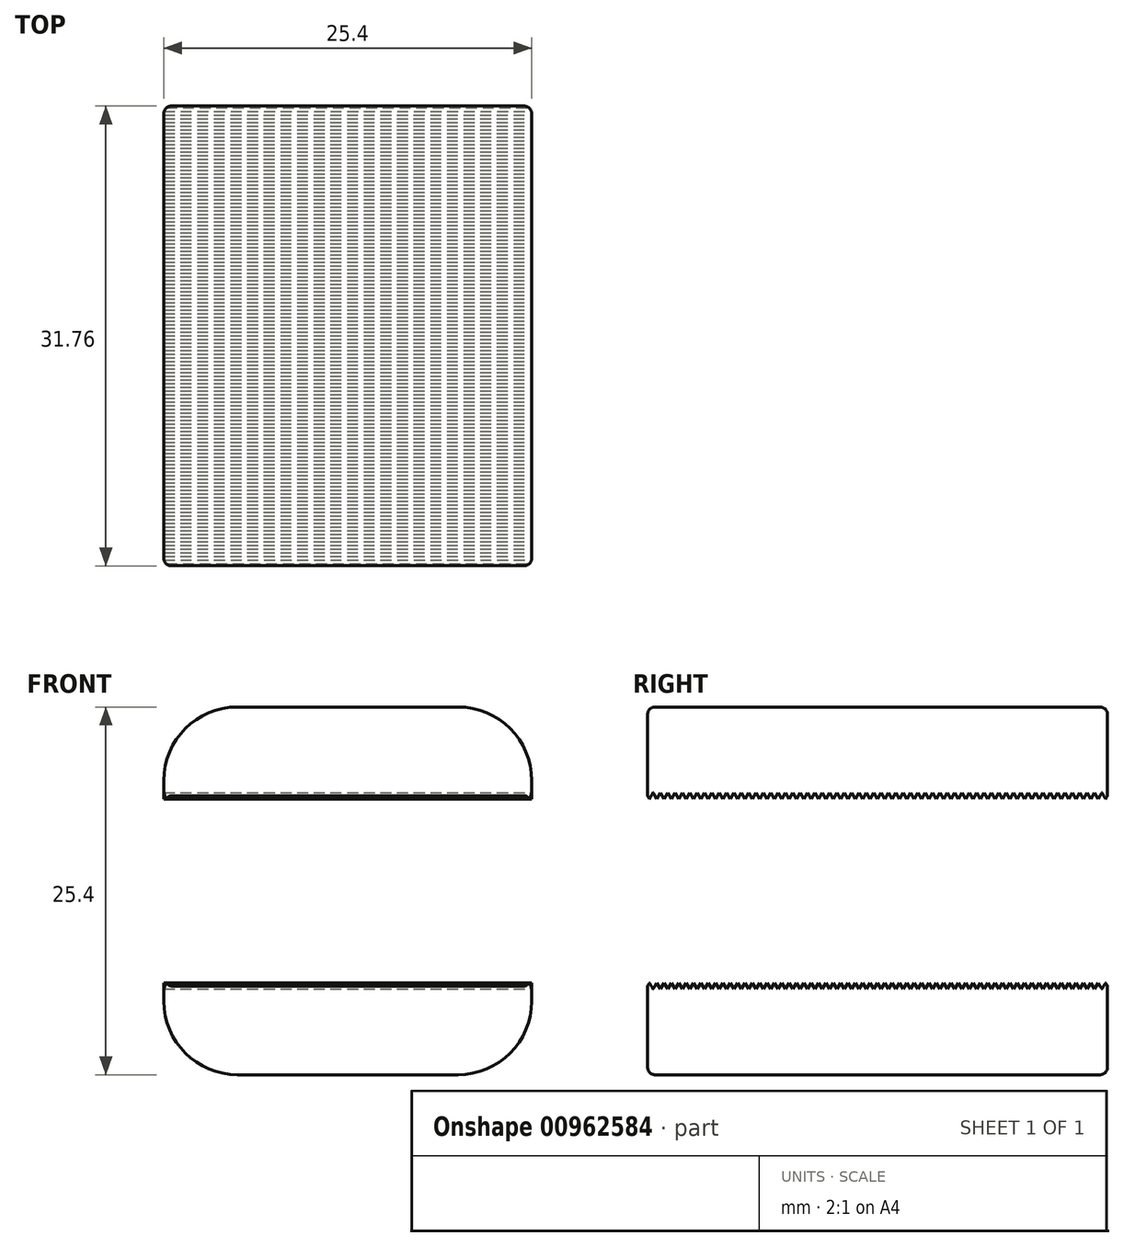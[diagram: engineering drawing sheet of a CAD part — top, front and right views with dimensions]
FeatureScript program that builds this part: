
annotation { "Feature Type Name" : "Feature", "Feature Type Description" : "" }
export const myFeature = defineFeature(function(context is Context, id is Id, definition is map)
    precondition{}
    {
        {
            var Q0;
            Q0=qCreatedBy(makeId("Front.planeOp"),FACE);
            var sketch = newSketch(context, id + "F0", { "sketchPlane" : qUnion([Q0])});
            skLineSegment(sketch, "E0.bottom", {"start": v(12.7, -12.7) * mm, "end": v(-12.7, -12.7) * mm});
            skLineSegment(sketch, "E0.top", {"start": v(12.7, 12.7) * mm, "end": v(-12.7, 12.7) * mm});
            skLineSegment(sketch, "E0.left", {"start": v(12.7, -12.7) * mm, "end": v(12.7, -6.35) * mm});
            skLineSegment(sketch, "E0.right", {"start": v(-12.7, -12.7) * mm, "end": v(-12.7, -6.35) * mm});
            skPoint(sketch, "E0.middle", {"position": v(0, 0) * mm});
            skLineSegment(sketch, "E1.bottom", {"start": v(12.7, -6.35) * mm, "end": v(-12.7, -6.35) * mm});
            skLineSegment(sketch, "E1.top", {"start": v(12.7, 6.35) * mm, "end": v(-12.7, 6.35) * mm});
            skLineSegment(sketch, "E2.trimOffspring", {"start": v(-12.7, 6.35) * mm, "end": v(-12.7, 12.7) * mm});
            skLineSegment(sketch, "E3.trimOffspring", {"start": v(12.7, 6.35) * mm, "end": v(12.7, 12.7) * mm});
            skSolve(sketch);
        }
        {
            var Q0;
            Q0=qSketchRegion(id+"F0",true);
            extrude(context, id + "F1", {"entities" : qUnion([Q0]), "endBound" : BoundingType.SYMMETRIC, "depth" : 31.75 * mm, "offsetDistance" : 25.4 * mm});
        }
        {
            var Q0;
            Q0=qCreatedBy(makeId("Right.planeOp"),FACE);
            var sketch = newSketch(context, id + "F2", { "sketchPlane" : qUnion([Q0])});
            skLineSegment(sketch, "E4", {"start": v(0, 6.35) * mm, "end": v(-0.25, 6.79) * mm});
            skLineSegment(sketch, "E5", {"start": v(-0.25, 6.79) * mm, "end": v(-0.5, 6.35) * mm});
            skLineSegment(sketch, "E6.1.0.0", {"start": v(-0.5, 6.35) * mm, "end": v(-0.76, 6.79) * mm});
            skLineSegment(sketch, "E6.1.0.1", {"start": v(-0.76, 6.79) * mm, "end": v(-1.02, 6.35) * mm});
            skLineSegment(sketch, "E6.2.0.0", {"start": v(-1.02, 6.35) * mm, "end": v(-1.27, 6.79) * mm});
            skLineSegment(sketch, "E6.2.0.1", {"start": v(-1.27, 6.79) * mm, "end": v(-1.52, 6.35) * mm});
            skLineSegment(sketch, "E6.3.0.0", {"start": v(-1.52, 6.35) * mm, "end": v(-1.78, 6.79) * mm});
            skLineSegment(sketch, "E6.3.0.1", {"start": v(-1.78, 6.79) * mm, "end": v(-2.03, 6.35) * mm});
            skLineSegment(sketch, "E6.4.0.0", {"start": v(-2.03, 6.35) * mm, "end": v(-2.29, 6.79) * mm});
            skLineSegment(sketch, "E6.4.0.1", {"start": v(-2.29, 6.79) * mm, "end": v(-2.54, 6.35) * mm});
            skLineSegment(sketch, "E6.5.0.0", {"start": v(-2.54, 6.35) * mm, "end": v(-2.8, 6.79) * mm});
            skLineSegment(sketch, "E6.5.0.1", {"start": v(-2.8, 6.79) * mm, "end": v(-3.05, 6.35) * mm});
            skLineSegment(sketch, "E6.6.0.0", {"start": v(-3.05, 6.35) * mm, "end": v(-3.3, 6.79) * mm});
            skLineSegment(sketch, "E6.6.0.1", {"start": v(-3.3, 6.79) * mm, "end": v(-3.56, 6.35) * mm});
            skLineSegment(sketch, "E6.7.0.0", {"start": v(-3.56, 6.35) * mm, "end": v(-3.81, 6.79) * mm});
            skLineSegment(sketch, "E6.7.0.1", {"start": v(-3.81, 6.79) * mm, "end": v(-4.06, 6.35) * mm});
            skLineSegment(sketch, "E6.8.0.0", {"start": v(-4.06, 6.35) * mm, "end": v(-4.32, 6.79) * mm});
            skLineSegment(sketch, "E6.8.0.1", {"start": v(-4.32, 6.79) * mm, "end": v(-4.57, 6.35) * mm});
            skLineSegment(sketch, "E6.9.0.0", {"start": v(-4.57, 6.35) * mm, "end": v(-4.83, 6.79) * mm});
            skLineSegment(sketch, "E6.9.0.1", {"start": v(-4.83, 6.79) * mm, "end": v(-5.08, 6.35) * mm});
            skLineSegment(sketch, "E6.10.0.0", {"start": v(-5.08, 6.35) * mm, "end": v(-5.33, 6.79) * mm});
            skLineSegment(sketch, "E6.10.0.1", {"start": v(-5.33, 6.79) * mm, "end": v(-5.59, 6.35) * mm});
            skLineSegment(sketch, "E6.11.0.0", {"start": v(-5.59, 6.35) * mm, "end": v(-5.84, 6.79) * mm});
            skLineSegment(sketch, "E6.11.0.1", {"start": v(-5.84, 6.79) * mm, "end": v(-6.1, 6.35) * mm});
            skLineSegment(sketch, "E6.12.0.0", {"start": v(-6.1, 6.35) * mm, "end": v(-6.35, 6.79) * mm});
            skLineSegment(sketch, "E6.12.0.1", {"start": v(-6.35, 6.79) * mm, "end": v(-6.6, 6.35) * mm});
            skLineSegment(sketch, "E6.13.0.0", {"start": v(-6.6, 6.35) * mm, "end": v(-6.86, 6.79) * mm});
            skLineSegment(sketch, "E6.13.0.1", {"start": v(-6.86, 6.79) * mm, "end": v(-7.11, 6.35) * mm});
            skLineSegment(sketch, "E6.14.0.0", {"start": v(-7.11, 6.35) * mm, "end": v(-7.37, 6.79) * mm});
            skLineSegment(sketch, "E6.14.0.1", {"start": v(-7.37, 6.79) * mm, "end": v(-7.62, 6.35) * mm});
            skLineSegment(sketch, "E6.15.0.0", {"start": v(-7.62, 6.35) * mm, "end": v(-7.87, 6.79) * mm});
            skLineSegment(sketch, "E6.15.0.1", {"start": v(-7.87, 6.79) * mm, "end": v(-8.13, 6.35) * mm});
            skLineSegment(sketch, "E6.16.0.0", {"start": v(-8.13, 6.35) * mm, "end": v(-8.38, 6.79) * mm});
            skLineSegment(sketch, "E6.16.0.1", {"start": v(-8.38, 6.79) * mm, "end": v(-8.64, 6.35) * mm});
            skLineSegment(sketch, "E6.17.0.0", {"start": v(-8.64, 6.35) * mm, "end": v(-8.9, 6.79) * mm});
            skLineSegment(sketch, "E6.17.0.1", {"start": v(-8.9, 6.79) * mm, "end": v(-9.14, 6.35) * mm});
            skLineSegment(sketch, "E6.18.0.0", {"start": v(-9.14, 6.35) * mm, "end": v(-9.4, 6.79) * mm});
            skLineSegment(sketch, "E6.18.0.1", {"start": v(-9.4, 6.79) * mm, "end": v(-9.65, 6.35) * mm});
            skLineSegment(sketch, "E6.19.0.0", {"start": v(-9.65, 6.35) * mm, "end": v(-9.9, 6.79) * mm});
            skLineSegment(sketch, "E6.19.0.1", {"start": v(-9.9, 6.79) * mm, "end": v(-10.16, 6.35) * mm});
            skLineSegment(sketch, "E6.20.0.0", {"start": v(-10.16, 6.35) * mm, "end": v(-10.41, 6.79) * mm});
            skLineSegment(sketch, "E6.20.0.1", {"start": v(-10.41, 6.79) * mm, "end": v(-10.67, 6.35) * mm});
            skLineSegment(sketch, "E6.21.0.0", {"start": v(-10.67, 6.35) * mm, "end": v(-10.92, 6.79) * mm});
            skLineSegment(sketch, "E6.21.0.1", {"start": v(-10.92, 6.79) * mm, "end": v(-11.18, 6.35) * mm});
            skLineSegment(sketch, "E6.22.0.0", {"start": v(-11.18, 6.35) * mm, "end": v(-11.43, 6.79) * mm});
            skLineSegment(sketch, "E6.22.0.1", {"start": v(-11.43, 6.79) * mm, "end": v(-11.68, 6.35) * mm});
            skLineSegment(sketch, "E6.23.0.0", {"start": v(-11.68, 6.35) * mm, "end": v(-11.94, 6.79) * mm});
            skLineSegment(sketch, "E6.23.0.1", {"start": v(-11.94, 6.79) * mm, "end": v(-12.2, 6.35) * mm});
            skLineSegment(sketch, "E6.24.0.0", {"start": v(-12.2, 6.35) * mm, "end": v(-12.45, 6.79) * mm});
            skLineSegment(sketch, "E6.24.0.1", {"start": v(-12.45, 6.79) * mm, "end": v(-12.7, 6.35) * mm});
            skLineSegment(sketch, "E6.direction1", {"start": v(-0.5, 6.35) * mm, "end": v(-1.02, 6.35) * mm, "construction": true});
            skLineSegment(sketch, "E7.0.25.0", {"start": v(-12.7, 6.35) * mm, "end": v(-12.95, 6.79) * mm});
            skLineSegment(sketch, "E7.3.25.0", {"start": v(-12.95, 6.79) * mm, "end": v(-13.2, 6.35) * mm});
            skLineSegment(sketch, "E7.0.26.0", {"start": v(-13.2, 6.35) * mm, "end": v(-13.46, 6.79) * mm});
            skLineSegment(sketch, "E7.3.26.0", {"start": v(-13.46, 6.79) * mm, "end": v(-13.72, 6.35) * mm});
            skLineSegment(sketch, "E7.0.27.0", {"start": v(-13.72, 6.35) * mm, "end": v(-13.97, 6.79) * mm});
            skLineSegment(sketch, "E7.3.27.0", {"start": v(-13.97, 6.79) * mm, "end": v(-14.22, 6.35) * mm});
            skLineSegment(sketch, "E7.0.28.0", {"start": v(-14.22, 6.35) * mm, "end": v(-14.48, 6.79) * mm});
            skLineSegment(sketch, "E7.3.28.0", {"start": v(-14.48, 6.79) * mm, "end": v(-14.73, 6.35) * mm});
            skLineSegment(sketch, "E7.0.29.0", {"start": v(-14.73, 6.35) * mm, "end": v(-14.99, 6.79) * mm});
            skLineSegment(sketch, "E7.3.29.0", {"start": v(-14.99, 6.79) * mm, "end": v(-15.24, 6.35) * mm});
            skLineSegment(sketch, "E7.0.30.0", {"start": v(-15.24, 6.35) * mm, "end": v(-15.5, 6.79) * mm});
            skLineSegment(sketch, "E7.3.30.0", {"start": v(-15.5, 6.79) * mm, "end": v(-15.75, 6.35) * mm});
            skLineSegment(sketch, "E7.0.31.0", {"start": v(-15.75, 6.35) * mm, "end": v(-16, 6.79) * mm});
            skLineSegment(sketch, "E7.3.31.0", {"start": v(-16, 6.79) * mm, "end": v(-16.26, 6.35) * mm});
            skLineSegment(sketch, "E7.0.32.0", {"start": v(-16.26, 6.35) * mm, "end": v(-16.51, 6.79) * mm});
            skLineSegment(sketch, "E7.3.32.0", {"start": v(-16.51, 6.79) * mm, "end": v(-16.76, 6.35) * mm});
            skLineSegment(sketch, "E7.0.33.0", {"start": v(-16.76, 6.35) * mm, "end": v(-17.02, 6.79) * mm});
            skLineSegment(sketch, "E7.3.33.0", {"start": v(-17.02, 6.79) * mm, "end": v(-17.27, 6.35) * mm});
            skLineSegment(sketch, "E7.0.34.0", {"start": v(-17.27, 6.35) * mm, "end": v(-17.53, 6.79) * mm});
            skLineSegment(sketch, "E7.3.34.0", {"start": v(-17.53, 6.79) * mm, "end": v(-17.78, 6.35) * mm});
            skLineSegment(sketch, "E7.0.35.0", {"start": v(-17.78, 6.35) * mm, "end": v(-18.03, 6.79) * mm});
            skLineSegment(sketch, "E7.3.35.0", {"start": v(-18.03, 6.79) * mm, "end": v(-18.29, 6.35) * mm});
            skLineSegment(sketch, "E7.0.36.0", {"start": v(-18.29, 6.35) * mm, "end": v(-18.54, 6.79) * mm});
            skLineSegment(sketch, "E7.3.36.0", {"start": v(-18.54, 6.79) * mm, "end": v(-18.8, 6.35) * mm});
            skLineSegment(sketch, "E7.0.37.0", {"start": v(-18.8, 6.35) * mm, "end": v(-19.05, 6.79) * mm});
            skLineSegment(sketch, "E7.3.37.0", {"start": v(-19.05, 6.79) * mm, "end": v(-19.3, 6.35) * mm});
            skLineSegment(sketch, "E7.0.38.0", {"start": v(-19.3, 6.35) * mm, "end": v(-19.56, 6.79) * mm});
            skLineSegment(sketch, "E7.3.38.0", {"start": v(-19.56, 6.79) * mm, "end": v(-19.81, 6.35) * mm});
            skLineSegment(sketch, "E7.0.39.0", {"start": v(-19.81, 6.35) * mm, "end": v(-20.07, 6.79) * mm});
            skLineSegment(sketch, "E7.3.39.0", {"start": v(-20.07, 6.79) * mm, "end": v(-20.32, 6.35) * mm});
            skLineSegment(sketch, "E8.1.0.0", {"start": v(0.25, 6.79) * mm, "end": v(0, 6.35) * mm});
            skLineSegment(sketch, "E8.1.0.1", {"start": v(0.5, 6.35) * mm, "end": v(0.25, 6.79) * mm});
            skLineSegment(sketch, "E8.2.0.0", {"start": v(0.76, 6.79) * mm, "end": v(0.5, 6.35) * mm});
            skLineSegment(sketch, "E8.2.0.1", {"start": v(1.02, 6.35) * mm, "end": v(0.76, 6.79) * mm});
            skLineSegment(sketch, "E8.3.0.0", {"start": v(1.27, 6.79) * mm, "end": v(1.02, 6.35) * mm});
            skLineSegment(sketch, "E8.3.0.1", {"start": v(1.52, 6.35) * mm, "end": v(1.27, 6.79) * mm});
            skLineSegment(sketch, "E8.4.0.0", {"start": v(1.78, 6.79) * mm, "end": v(1.52, 6.35) * mm});
            skLineSegment(sketch, "E8.4.0.1", {"start": v(2.03, 6.35) * mm, "end": v(1.78, 6.79) * mm});
            skLineSegment(sketch, "E8.5.0.0", {"start": v(2.29, 6.79) * mm, "end": v(2.03, 6.35) * mm});
            skLineSegment(sketch, "E8.5.0.1", {"start": v(2.54, 6.35) * mm, "end": v(2.29, 6.79) * mm});
            skLineSegment(sketch, "E8.6.0.0", {"start": v(2.8, 6.79) * mm, "end": v(2.54, 6.35) * mm});
            skLineSegment(sketch, "E8.6.0.1", {"start": v(3.05, 6.35) * mm, "end": v(2.8, 6.79) * mm});
            skLineSegment(sketch, "E8.7.0.0", {"start": v(3.3, 6.79) * mm, "end": v(3.05, 6.35) * mm});
            skLineSegment(sketch, "E8.7.0.1", {"start": v(3.56, 6.35) * mm, "end": v(3.3, 6.79) * mm});
            skLineSegment(sketch, "E8.8.0.0", {"start": v(3.81, 6.79) * mm, "end": v(3.56, 6.35) * mm});
            skLineSegment(sketch, "E8.8.0.1", {"start": v(4.06, 6.35) * mm, "end": v(3.81, 6.79) * mm});
            skLineSegment(sketch, "E8.9.0.0", {"start": v(4.32, 6.79) * mm, "end": v(4.06, 6.35) * mm});
            skLineSegment(sketch, "E8.9.0.1", {"start": v(4.57, 6.35) * mm, "end": v(4.32, 6.79) * mm});
            skLineSegment(sketch, "E8.10.0.0", {"start": v(4.83, 6.79) * mm, "end": v(4.57, 6.35) * mm});
            skLineSegment(sketch, "E8.10.0.1", {"start": v(5.08, 6.35) * mm, "end": v(4.83, 6.79) * mm});
            skLineSegment(sketch, "E8.11.0.0", {"start": v(5.33, 6.79) * mm, "end": v(5.08, 6.35) * mm});
            skLineSegment(sketch, "E8.11.0.1", {"start": v(5.59, 6.35) * mm, "end": v(5.33, 6.79) * mm});
            skLineSegment(sketch, "E8.12.0.0", {"start": v(5.84, 6.79) * mm, "end": v(5.59, 6.35) * mm});
            skLineSegment(sketch, "E8.12.0.1", {"start": v(6.1, 6.35) * mm, "end": v(5.84, 6.79) * mm});
            skLineSegment(sketch, "E8.13.0.0", {"start": v(6.35, 6.79) * mm, "end": v(6.1, 6.35) * mm});
            skLineSegment(sketch, "E8.13.0.1", {"start": v(6.6, 6.35) * mm, "end": v(6.35, 6.79) * mm});
            skLineSegment(sketch, "E8.14.0.0", {"start": v(6.86, 6.79) * mm, "end": v(6.6, 6.35) * mm});
            skLineSegment(sketch, "E8.14.0.1", {"start": v(7.11, 6.35) * mm, "end": v(6.86, 6.79) * mm});
            skLineSegment(sketch, "E8.15.0.0", {"start": v(7.37, 6.79) * mm, "end": v(7.11, 6.35) * mm});
            skLineSegment(sketch, "E8.15.0.1", {"start": v(7.62, 6.35) * mm, "end": v(7.37, 6.79) * mm});
            skLineSegment(sketch, "E8.16.0.0", {"start": v(7.87, 6.79) * mm, "end": v(7.62, 6.35) * mm});
            skLineSegment(sketch, "E8.16.0.1", {"start": v(8.13, 6.35) * mm, "end": v(7.87, 6.79) * mm});
            skLineSegment(sketch, "E8.17.0.0", {"start": v(8.38, 6.79) * mm, "end": v(8.13, 6.35) * mm});
            skLineSegment(sketch, "E8.17.0.1", {"start": v(8.64, 6.35) * mm, "end": v(8.38, 6.79) * mm});
            skLineSegment(sketch, "E8.18.0.0", {"start": v(8.9, 6.79) * mm, "end": v(8.64, 6.35) * mm});
            skLineSegment(sketch, "E8.18.0.1", {"start": v(9.14, 6.35) * mm, "end": v(8.9, 6.79) * mm});
            skLineSegment(sketch, "E8.19.0.0", {"start": v(9.4, 6.79) * mm, "end": v(9.14, 6.35) * mm});
            skLineSegment(sketch, "E8.19.0.1", {"start": v(9.65, 6.35) * mm, "end": v(9.4, 6.79) * mm});
            skLineSegment(sketch, "E8.20.0.0", {"start": v(9.9, 6.79) * mm, "end": v(9.65, 6.35) * mm});
            skLineSegment(sketch, "E8.20.0.1", {"start": v(10.16, 6.35) * mm, "end": v(9.9, 6.79) * mm});
            skLineSegment(sketch, "E8.21.0.0", {"start": v(10.41, 6.79) * mm, "end": v(10.16, 6.35) * mm});
            skLineSegment(sketch, "E8.21.0.1", {"start": v(10.67, 6.35) * mm, "end": v(10.41, 6.79) * mm});
            skLineSegment(sketch, "E8.22.0.0", {"start": v(10.92, 6.79) * mm, "end": v(10.67, 6.35) * mm});
            skLineSegment(sketch, "E8.22.0.1", {"start": v(11.18, 6.35) * mm, "end": v(10.92, 6.79) * mm});
            skLineSegment(sketch, "E8.23.0.0", {"start": v(11.43, 6.79) * mm, "end": v(11.18, 6.35) * mm});
            skLineSegment(sketch, "E8.23.0.1", {"start": v(11.68, 6.35) * mm, "end": v(11.43, 6.79) * mm});
            skLineSegment(sketch, "E8.24.0.0", {"start": v(11.94, 6.79) * mm, "end": v(11.68, 6.35) * mm});
            skLineSegment(sketch, "E8.24.0.1", {"start": v(12.2, 6.35) * mm, "end": v(11.94, 6.79) * mm});
            skLineSegment(sketch, "E8.25.0.0", {"start": v(12.45, 6.79) * mm, "end": v(12.2, 6.35) * mm});
            skLineSegment(sketch, "E8.25.0.1", {"start": v(12.7, 6.35) * mm, "end": v(12.45, 6.79) * mm});
            skLineSegment(sketch, "E8.26.0.0", {"start": v(12.95, 6.79) * mm, "end": v(12.7, 6.35) * mm});
            skLineSegment(sketch, "E8.26.0.1", {"start": v(13.2, 6.35) * mm, "end": v(12.95, 6.79) * mm});
            skLineSegment(sketch, "E8.27.0.0", {"start": v(13.46, 6.79) * mm, "end": v(13.2, 6.35) * mm});
            skLineSegment(sketch, "E8.27.0.1", {"start": v(13.72, 6.35) * mm, "end": v(13.46, 6.79) * mm});
            skLineSegment(sketch, "E8.28.0.0", {"start": v(13.97, 6.79) * mm, "end": v(13.72, 6.35) * mm});
            skLineSegment(sketch, "E8.28.0.1", {"start": v(14.22, 6.35) * mm, "end": v(13.97, 6.79) * mm});
            skLineSegment(sketch, "E8.29.0.0", {"start": v(14.48, 6.79) * mm, "end": v(14.22, 6.35) * mm});
            skLineSegment(sketch, "E8.29.0.1", {"start": v(14.73, 6.35) * mm, "end": v(14.48, 6.79) * mm});
            skLineSegment(sketch, "E8.30.0.0", {"start": v(14.99, 6.79) * mm, "end": v(14.73, 6.35) * mm});
            skLineSegment(sketch, "E8.30.0.1", {"start": v(15.24, 6.35) * mm, "end": v(14.99, 6.79) * mm});
            skLineSegment(sketch, "E8.31.0.0", {"start": v(15.5, 6.79) * mm, "end": v(15.24, 6.35) * mm});
            skLineSegment(sketch, "E8.31.0.1", {"start": v(15.75, 6.35) * mm, "end": v(15.5, 6.79) * mm});
            skLineSegment(sketch, "E8.32.0.0", {"start": v(16, 6.79) * mm, "end": v(15.75, 6.35) * mm});
            skLineSegment(sketch, "E8.32.0.1", {"start": v(16.26, 6.35) * mm, "end": v(16, 6.79) * mm});
            skLineSegment(sketch, "E8.33.0.0", {"start": v(16.51, 6.79) * mm, "end": v(16.26, 6.35) * mm});
            skLineSegment(sketch, "E8.33.0.1", {"start": v(16.76, 6.35) * mm, "end": v(16.51, 6.79) * mm});
            skLineSegment(sketch, "E8.34.0.0", {"start": v(17.02, 6.79) * mm, "end": v(16.76, 6.35) * mm});
            skLineSegment(sketch, "E8.34.0.1", {"start": v(17.27, 6.35) * mm, "end": v(17.02, 6.79) * mm});
            skLineSegment(sketch, "E8.35.0.0", {"start": v(17.53, 6.79) * mm, "end": v(17.27, 6.35) * mm});
            skLineSegment(sketch, "E8.35.0.1", {"start": v(17.78, 6.35) * mm, "end": v(17.53, 6.79) * mm});
            skLineSegment(sketch, "E8.36.0.0", {"start": v(18.03, 6.79) * mm, "end": v(17.78, 6.35) * mm});
            skLineSegment(sketch, "E8.36.0.1", {"start": v(18.29, 6.35) * mm, "end": v(18.03, 6.79) * mm});
            skLineSegment(sketch, "E8.37.0.0", {"start": v(18.54, 6.79) * mm, "end": v(18.29, 6.35) * mm});
            skLineSegment(sketch, "E8.37.0.1", {"start": v(18.8, 6.35) * mm, "end": v(18.54, 6.79) * mm});
            skLineSegment(sketch, "E8.38.0.0", {"start": v(19.05, 6.79) * mm, "end": v(18.8, 6.35) * mm});
            skLineSegment(sketch, "E8.38.0.1", {"start": v(19.3, 6.35) * mm, "end": v(19.05, 6.79) * mm});
            skLineSegment(sketch, "E8.39.0.0", {"start": v(19.56, 6.79) * mm, "end": v(19.3, 6.35) * mm});
            skLineSegment(sketch, "E8.39.0.1", {"start": v(19.81, 6.35) * mm, "end": v(19.56, 6.79) * mm});
            skLineSegment(sketch, "E8.40.0.0", {"start": v(20.07, 6.79) * mm, "end": v(19.81, 6.35) * mm});
            skLineSegment(sketch, "E8.40.0.1", {"start": v(20.32, 6.35) * mm, "end": v(20.07, 6.79) * mm});
            skLineSegment(sketch, "E8.direction1", {"start": v(-0.5, 6.35) * mm, "end": v(0, 6.35) * mm, "construction": true});
            skLineSegment(sketch, "E9.0.41.0", {"start": v(20.57, 6.79) * mm, "end": v(20.32, 6.35) * mm});
            skLineSegment(sketch, "E9.3.41.0", {"start": v(20.83, 6.35) * mm, "end": v(20.57, 6.79) * mm});
            skLineSegment(sketch, "E9.0.42.0", {"start": v(21.08, 6.79) * mm, "end": v(20.83, 6.35) * mm});
            skLineSegment(sketch, "E9.3.42.0", {"start": v(21.34, 6.35) * mm, "end": v(21.08, 6.79) * mm});
            skLineSegment(sketch, "E9.0.43.0", {"start": v(21.6, 6.79) * mm, "end": v(21.34, 6.35) * mm});
            skLineSegment(sketch, "E9.3.43.0", {"start": v(21.84, 6.35) * mm, "end": v(21.59, 6.79) * mm});
            skLineSegment(sketch, "E9.0.44.0", {"start": v(22.1, 6.79) * mm, "end": v(21.84, 6.35) * mm});
            skLineSegment(sketch, "E9.3.44.0", {"start": v(22.35, 6.35) * mm, "end": v(22.1, 6.79) * mm});
            skLineSegment(sketch, "E9.0.45.0", {"start": v(22.6, 6.79) * mm, "end": v(22.35, 6.35) * mm});
            skLineSegment(sketch, "E9.3.45.0", {"start": v(22.86, 6.35) * mm, "end": v(22.6, 6.79) * mm});
            skLineSegment(sketch, "E9.0.46.0", {"start": v(23.11, 6.79) * mm, "end": v(22.86, 6.35) * mm});
            skLineSegment(sketch, "E9.3.46.0", {"start": v(23.37, 6.35) * mm, "end": v(23.11, 6.79) * mm});
            skLineSegment(sketch, "E9.0.47.0", {"start": v(23.62, 6.79) * mm, "end": v(23.37, 6.35) * mm});
            skLineSegment(sketch, "E9.3.47.0", {"start": v(23.88, 6.35) * mm, "end": v(23.62, 6.79) * mm});
            skLineSegment(sketch, "E9.0.48.0", {"start": v(24.13, 6.79) * mm, "end": v(23.88, 6.35) * mm});
            skLineSegment(sketch, "E9.3.48.0", {"start": v(24.38, 6.35) * mm, "end": v(24.13, 6.79) * mm});
            skLineSegment(sketch, "E9.0.49.0", {"start": v(24.64, 6.79) * mm, "end": v(24.38, 6.35) * mm});
            skLineSegment(sketch, "E9.3.49.0", {"start": v(24.9, 6.35) * mm, "end": v(24.64, 6.79) * mm});
            skLineSegment(sketch, "E9.0.50.0", {"start": v(25.15, 6.79) * mm, "end": v(24.9, 6.35) * mm});
            skLineSegment(sketch, "E9.3.50.0", {"start": v(25.4, 6.35) * mm, "end": v(25.15, 6.79) * mm});
            skLineSegment(sketch, "E9.0.51.0", {"start": v(25.65, 6.79) * mm, "end": v(25.4, 6.35) * mm});
            skLineSegment(sketch, "E9.3.51.0", {"start": v(25.9, 6.35) * mm, "end": v(25.65, 6.79) * mm});
            skLineSegment(sketch, "E9.0.52.0", {"start": v(26.16, 6.79) * mm, "end": v(25.9, 6.35) * mm});
            skLineSegment(sketch, "E9.3.52.0", {"start": v(26.42, 6.35) * mm, "end": v(26.16, 6.79) * mm});
            skLineSegment(sketch, "E9.0.53.0", {"start": v(26.67, 6.79) * mm, "end": v(26.42, 6.35) * mm});
            skLineSegment(sketch, "E9.3.53.0", {"start": v(26.92, 6.35) * mm, "end": v(26.67, 6.79) * mm});
            skLineSegment(sketch, "E9.0.54.0", {"start": v(27.18, 6.79) * mm, "end": v(26.92, 6.35) * mm});
            skLineSegment(sketch, "E9.3.54.0", {"start": v(27.43, 6.35) * mm, "end": v(27.18, 6.79) * mm});
            skLineSegment(sketch, "E9.0.55.0", {"start": v(27.69, 6.79) * mm, "end": v(27.43, 6.35) * mm});
            skLineSegment(sketch, "E9.3.55.0", {"start": v(27.94, 6.35) * mm, "end": v(27.69, 6.79) * mm});
            skLineSegment(sketch, "E9.0.56.0", {"start": v(28.2, 6.79) * mm, "end": v(27.94, 6.35) * mm});
            skLineSegment(sketch, "E9.3.56.0", {"start": v(28.45, 6.35) * mm, "end": v(28.2, 6.79) * mm});
            skLineSegment(sketch, "E9.0.57.0", {"start": v(28.7, 6.79) * mm, "end": v(28.45, 6.35) * mm});
            skLineSegment(sketch, "E9.3.57.0", {"start": v(28.96, 6.35) * mm, "end": v(28.7, 6.79) * mm});
            skLineSegment(sketch, "E9.0.58.0", {"start": v(29.21, 6.79) * mm, "end": v(28.96, 6.35) * mm});
            skLineSegment(sketch, "E9.3.58.0", {"start": v(29.46, 6.35) * mm, "end": v(29.21, 6.79) * mm});
            skLineSegment(sketch, "E9.0.59.0", {"start": v(29.72, 6.79) * mm, "end": v(29.46, 6.35) * mm});
            skLineSegment(sketch, "E9.3.59.0", {"start": v(29.97, 6.35) * mm, "end": v(29.72, 6.79) * mm});
            skLineSegment(sketch, "E9.0.60.0", {"start": v(30.23, 6.79) * mm, "end": v(29.97, 6.35) * mm});
            skLineSegment(sketch, "E9.3.60.0", {"start": v(30.48, 6.35) * mm, "end": v(30.23, 6.79) * mm});
            skLineSegment(sketch, "E9.0.61.0", {"start": v(30.73, 6.79) * mm, "end": v(30.48, 6.35) * mm});
            skLineSegment(sketch, "E9.3.61.0", {"start": v(30.99, 6.35) * mm, "end": v(30.73, 6.79) * mm});
            skLineSegment(sketch, "E10.0.40.0", {"start": v(-20.32, 6.35) * mm, "end": v(-20.57, 6.79) * mm});
            skLineSegment(sketch, "E10.3.40.0", {"start": v(-20.57, 6.79) * mm, "end": v(-20.83, 6.35) * mm});
            skLineSegment(sketch, "E10.0.41.0", {"start": v(-20.83, 6.35) * mm, "end": v(-21.08, 6.79) * mm});
            skLineSegment(sketch, "E10.3.41.0", {"start": v(-21.08, 6.79) * mm, "end": v(-21.34, 6.35) * mm});
            skLineSegment(sketch, "E10.0.42.0", {"start": v(-21.34, 6.35) * mm, "end": v(-21.6, 6.79) * mm});
            skLineSegment(sketch, "E10.3.42.0", {"start": v(-21.59, 6.79) * mm, "end": v(-21.84, 6.35) * mm});
            skLineSegment(sketch, "E10.0.43.0", {"start": v(-21.84, 6.35) * mm, "end": v(-22.1, 6.79) * mm});
            skLineSegment(sketch, "E10.3.43.0", {"start": v(-22.1, 6.79) * mm, "end": v(-22.35, 6.35) * mm});
            skLineSegment(sketch, "E10.0.44.0", {"start": v(-22.35, 6.35) * mm, "end": v(-22.6, 6.79) * mm});
            skLineSegment(sketch, "E10.3.44.0", {"start": v(-22.6, 6.79) * mm, "end": v(-22.86, 6.35) * mm});
            skLineSegment(sketch, "E10.0.45.0", {"start": v(-22.86, 6.35) * mm, "end": v(-23.11, 6.79) * mm});
            skLineSegment(sketch, "E10.3.45.0", {"start": v(-23.11, 6.79) * mm, "end": v(-23.37, 6.35) * mm});
            skLineSegment(sketch, "E10.0.46.0", {"start": v(-23.37, 6.35) * mm, "end": v(-23.62, 6.79) * mm});
            skLineSegment(sketch, "E10.3.46.0", {"start": v(-23.62, 6.79) * mm, "end": v(-23.88, 6.35) * mm});
            skLineSegment(sketch, "E10.0.47.0", {"start": v(-23.88, 6.35) * mm, "end": v(-24.13, 6.79) * mm});
            skLineSegment(sketch, "E10.3.47.0", {"start": v(-24.13, 6.79) * mm, "end": v(-24.38, 6.35) * mm});
            skLineSegment(sketch, "E10.0.48.0", {"start": v(-24.38, 6.35) * mm, "end": v(-24.64, 6.79) * mm});
            skLineSegment(sketch, "E10.3.48.0", {"start": v(-24.64, 6.79) * mm, "end": v(-24.9, 6.35) * mm});
            skLineSegment(sketch, "E10.0.49.0", {"start": v(-24.9, 6.35) * mm, "end": v(-25.15, 6.79) * mm});
            skLineSegment(sketch, "E10.3.49.0", {"start": v(-25.15, 6.79) * mm, "end": v(-25.4, 6.35) * mm});
            skLineSegment(sketch, "E10.0.50.0", {"start": v(-25.4, 6.35) * mm, "end": v(-25.65, 6.79) * mm});
            skLineSegment(sketch, "E10.3.50.0", {"start": v(-25.65, 6.79) * mm, "end": v(-25.9, 6.35) * mm});
            skLineSegment(sketch, "E10.0.51.0", {"start": v(-25.9, 6.35) * mm, "end": v(-26.16, 6.79) * mm});
            skLineSegment(sketch, "E10.3.51.0", {"start": v(-26.16, 6.79) * mm, "end": v(-26.42, 6.35) * mm});
            skLineSegment(sketch, "E10.0.52.0", {"start": v(-26.42, 6.35) * mm, "end": v(-26.67, 6.79) * mm});
            skLineSegment(sketch, "E10.3.52.0", {"start": v(-26.67, 6.79) * mm, "end": v(-26.92, 6.35) * mm});
            skLineSegment(sketch, "E10.0.53.0", {"start": v(-26.92, 6.35) * mm, "end": v(-27.18, 6.79) * mm});
            skLineSegment(sketch, "E10.3.53.0", {"start": v(-27.18, 6.79) * mm, "end": v(-27.43, 6.35) * mm});
            skLineSegment(sketch, "E10.0.54.0", {"start": v(-27.43, 6.35) * mm, "end": v(-27.69, 6.79) * mm});
            skLineSegment(sketch, "E10.3.54.0", {"start": v(-27.69, 6.79) * mm, "end": v(-27.94, 6.35) * mm});
            skLineSegment(sketch, "E10.0.55.0", {"start": v(-27.94, 6.35) * mm, "end": v(-28.2, 6.79) * mm});
            skLineSegment(sketch, "E10.3.55.0", {"start": v(-28.2, 6.79) * mm, "end": v(-28.45, 6.35) * mm});
            skLineSegment(sketch, "E10.0.56.0", {"start": v(-28.45, 6.35) * mm, "end": v(-28.7, 6.79) * mm});
            skLineSegment(sketch, "E10.3.56.0", {"start": v(-28.7, 6.79) * mm, "end": v(-28.96, 6.35) * mm});
            skLineSegment(sketch, "E10.0.57.0", {"start": v(-28.96, 6.35) * mm, "end": v(-29.21, 6.79) * mm});
            skLineSegment(sketch, "E10.3.57.0", {"start": v(-29.21, 6.79) * mm, "end": v(-29.46, 6.35) * mm});
            skLineSegment(sketch, "E10.0.58.0", {"start": v(-29.46, 6.35) * mm, "end": v(-29.72, 6.79) * mm});
            skLineSegment(sketch, "E10.3.58.0", {"start": v(-29.72, 6.79) * mm, "end": v(-29.97, 6.35) * mm});
            skLineSegment(sketch, "E10.0.59.0", {"start": v(-29.97, 6.35) * mm, "end": v(-30.23, 6.79) * mm});
            skLineSegment(sketch, "E10.3.59.0", {"start": v(-30.23, 6.79) * mm, "end": v(-30.48, 6.35) * mm});
            skLineSegment(sketch, "E10.0.60.0", {"start": v(-30.48, 6.35) * mm, "end": v(-30.73, 6.79) * mm});
            skLineSegment(sketch, "E10.3.60.0", {"start": v(-30.73, 6.79) * mm, "end": v(-30.99, 6.35) * mm});
            skLineSegment(sketch, "E10.0.61.0", {"start": v(-30.99, 6.35) * mm, "end": v(-31.24, 6.79) * mm});
            skLineSegment(sketch, "E10.3.61.0", {"start": v(-31.24, 6.79) * mm, "end": v(-31.5, 6.35) * mm});
            skLineSegment(sketch, "E10.0.62.0", {"start": v(-31.5, 6.35) * mm, "end": v(-31.75, 6.79) * mm});
            skLineSegment(sketch, "E10.3.62.0", {"start": v(-31.75, 6.79) * mm, "end": v(-32, 6.35) * mm});
            skLineSegment(sketch, "E10.0.63.0", {"start": v(-32, 6.35) * mm, "end": v(-32.26, 6.79) * mm});
            skLineSegment(sketch, "E10.3.63.0", {"start": v(-32.26, 6.79) * mm, "end": v(-32.51, 6.35) * mm});
            skLineSegment(sketch, "E11.0.62.0", {"start": v(31.24, 6.79) * mm, "end": v(30.99, 6.35) * mm});
            skLineSegment(sketch, "E11.3.62.0", {"start": v(31.5, 6.35) * mm, "end": v(31.24, 6.79) * mm});
            skLineSegment(sketch, "E12.0.63.0", {"start": v(31.75, 6.79) * mm, "end": v(31.5, 6.35) * mm});
            skLineSegment(sketch, "E12.3.63.0", {"start": v(32, 6.35) * mm, "end": v(31.75, 6.79) * mm});
            skLineSegment(sketch, "E12.0.64.0", {"start": v(32.26, 6.79) * mm, "end": v(32, 6.35) * mm});
            skLineSegment(sketch, "E12.3.64.0", {"start": v(32.51, 6.35) * mm, "end": v(32.26, 6.79) * mm});
            skLineSegment(sketch, "E13", {"start": v(-32.51, 6.35) * mm, "end": v(-32.51, 6.1) * mm});
            skLineSegment(sketch, "E14", {"start": v(-32.51, 6.1) * mm, "end": v(32.51, 6.1) * mm});
            skLineSegment(sketch, "E15", {"start": v(32.51, 6.1) * mm, "end": v(32.51, 6.35) * mm});
            skLineSegment(sketch, "E16.MirrorCS", {"start": v(19.56, -6.79) * mm, "end": v(19.3, -6.35) * mm});
            skLineSegment(sketch, "E17.MirrorCS", {"start": v(0, -6.35) * mm, "end": v(-0.25, -6.79) * mm});
            skLineSegment(sketch, "E18.MirrorCS", {"start": v(2.8, -6.79) * mm, "end": v(2.54, -6.35) * mm});
            skLineSegment(sketch, "E19.MirrorCS", {"start": v(19.05, -6.79) * mm, "end": v(18.8, -6.35) * mm});
            skLineSegment(sketch, "E20.MirrorCS", {"start": v(-28.7, -6.79) * mm, "end": v(-28.96, -6.35) * mm});
            skLineSegment(sketch, "E21.MirrorCS", {"start": v(-1.02, -6.35) * mm, "end": v(-1.27, -6.79) * mm});
            skLineSegment(sketch, "E22.MirrorCS", {"start": v(1.02, -6.35) * mm, "end": v(0.76, -6.79) * mm});
            skLineSegment(sketch, "E23.MirrorCS", {"start": v(3.3, -6.79) * mm, "end": v(3.05, -6.35) * mm});
            skLineSegment(sketch, "E24.MirrorCS", {"start": v(-28.2, -6.79) * mm, "end": v(-28.45, -6.35) * mm});
            skLineSegment(sketch, "E25.MirrorCS", {"start": v(5.08, -6.35) * mm, "end": v(4.83, -6.79) * mm});
            skLineSegment(sketch, "E26.MirrorCS", {"start": v(2.54, -6.35) * mm, "end": v(2.29, -6.79) * mm});
            skLineSegment(sketch, "E27.MirrorCS", {"start": v(-12.2, -6.35) * mm, "end": v(-12.45, -6.79) * mm});
            skLineSegment(sketch, "E28.MirrorCS", {"start": v(20.32, -6.35) * mm, "end": v(20.07, -6.79) * mm});
            skLineSegment(sketch, "E29.MirrorCS", {"start": v(-0.5, -6.35) * mm, "end": v(0, -6.35) * mm, "construction": true});
            skLineSegment(sketch, "E30.MirrorCS", {"start": v(-0.5, -6.35) * mm, "end": v(-1.02, -6.35) * mm, "construction": true});
            skLineSegment(sketch, "E31.MirrorCS", {"start": v(-17.02, -6.79) * mm, "end": v(-17.27, -6.35) * mm});
            skLineSegment(sketch, "E32.MirrorCS", {"start": v(5.59, -6.35) * mm, "end": v(5.33, -6.79) * mm});
            skLineSegment(sketch, "E33.MirrorCS", {"start": v(0.76, -6.79) * mm, "end": v(0.5, -6.35) * mm});
            skLineSegment(sketch, "E34.MirrorCS", {"start": v(2.29, -6.79) * mm, "end": v(2.03, -6.35) * mm});
            skLineSegment(sketch, "E35.MirrorCS", {"start": v(-4.06, -6.35) * mm, "end": v(-4.32, -6.79) * mm});
            skLineSegment(sketch, "E36.MirrorCS", {"start": v(4.57, -6.35) * mm, "end": v(4.32, -6.79) * mm});
            skLineSegment(sketch, "E37.MirrorCS", {"start": v(-27.94, -6.35) * mm, "end": v(-28.2, -6.79) * mm});
            skLineSegment(sketch, "E38.MirrorCS", {"start": v(-0.5, -6.35) * mm, "end": v(-0.76, -6.79) * mm});
            skLineSegment(sketch, "E39.MirrorCS", {"start": v(26.92, -6.35) * mm, "end": v(26.67, -6.79) * mm});
            skLineSegment(sketch, "E40.MirrorCS", {"start": v(3.05, -6.35) * mm, "end": v(2.8, -6.79) * mm});
            skLineSegment(sketch, "E41.MirrorCS", {"start": v(-0.76, -6.79) * mm, "end": v(-1.02, -6.35) * mm});
            skLineSegment(sketch, "E42.MirrorCS", {"start": v(-24.64, -6.79) * mm, "end": v(-24.9, -6.35) * mm});
            skLineSegment(sketch, "E43.MirrorCS", {"start": v(9.14, -6.35) * mm, "end": v(8.9, -6.79) * mm});
            skLineSegment(sketch, "E44.MirrorCS", {"start": v(-24.13, -6.79) * mm, "end": v(-24.38, -6.35) * mm});
            skLineSegment(sketch, "E45.MirrorCS", {"start": v(17.27, -6.35) * mm, "end": v(17.02, -6.79) * mm});
            skLineSegment(sketch, "E46.MirrorCS", {"start": v(-11.43, -6.79) * mm, "end": v(-11.68, -6.35) * mm});
            skLineSegment(sketch, "E47.MirrorCS", {"start": v(1.78, -6.79) * mm, "end": v(1.52, -6.35) * mm});
            skLineSegment(sketch, "E48.MirrorCS", {"start": v(-9.14, -6.35) * mm, "end": v(-9.4, -6.79) * mm});
            skLineSegment(sketch, "E49.MirrorCS", {"start": v(-12.95, -6.79) * mm, "end": v(-13.2, -6.35) * mm});
            skLineSegment(sketch, "E50.MirrorCS", {"start": v(11.43, -6.79) * mm, "end": v(11.18, -6.35) * mm});
            skLineSegment(sketch, "E51.MirrorCS", {"start": v(31.5, -6.35) * mm, "end": v(31.24, -6.79) * mm});
            skLineSegment(sketch, "E52.MirrorCS", {"start": v(15.5, -6.79) * mm, "end": v(15.24, -6.35) * mm});
            skLineSegment(sketch, "E53.MirrorCS", {"start": v(5.84, -6.79) * mm, "end": v(5.59, -6.35) * mm});
            skLineSegment(sketch, "E54.MirrorCS", {"start": v(0.5, -6.35) * mm, "end": v(0.25, -6.79) * mm});
            skLineSegment(sketch, "E55.MirrorCS", {"start": v(-15.24, -6.35) * mm, "end": v(-15.5, -6.79) * mm});
            skLineSegment(sketch, "E56.MirrorCS", {"start": v(19.3, -6.35) * mm, "end": v(19.05, -6.79) * mm});
            skLineSegment(sketch, "E57.MirrorCS", {"start": v(14.99, -6.79) * mm, "end": v(14.73, -6.35) * mm});
            skLineSegment(sketch, "E58.MirrorCS", {"start": v(4.83, -6.79) * mm, "end": v(4.57, -6.35) * mm});
            skLineSegment(sketch, "E59.MirrorCS", {"start": v(-27.69, -6.79) * mm, "end": v(-27.94, -6.35) * mm});
            skLineSegment(sketch, "E60.MirrorCS", {"start": v(1.27, -6.79) * mm, "end": v(1.02, -6.35) * mm});
            skLineSegment(sketch, "E61.MirrorCS", {"start": v(-8.13, -6.35) * mm, "end": v(-8.38, -6.79) * mm});
            skLineSegment(sketch, "E62.MirrorCS", {"start": v(27.43, -6.35) * mm, "end": v(27.18, -6.79) * mm});
            skLineSegment(sketch, "E63.MirrorCS", {"start": v(5.33, -6.79) * mm, "end": v(5.08, -6.35) * mm});
            skLineSegment(sketch, "E64.MirrorCS", {"start": v(19.81, -6.35) * mm, "end": v(19.56, -6.79) * mm});
            skLineSegment(sketch, "E65.MirrorCS", {"start": v(-14.73, -6.35) * mm, "end": v(-14.99, -6.79) * mm});
            skLineSegment(sketch, "E66.MirrorCS", {"start": v(-28.45, -6.35) * mm, "end": v(-28.7, -6.79) * mm});
            skLineSegment(sketch, "E67.MirrorCS", {"start": v(-7.37, -6.79) * mm, "end": v(-7.62, -6.35) * mm});
            skLineSegment(sketch, "E68.MirrorCS", {"start": v(-5.08, -6.35) * mm, "end": v(-5.33, -6.79) * mm});
            skLineSegment(sketch, "E69.MirrorCS", {"start": v(25.15, -6.79) * mm, "end": v(24.9, -6.35) * mm});
            skLineSegment(sketch, "E70.MirrorCS", {"start": v(-22.35, -6.35) * mm, "end": v(-22.6, -6.79) * mm});
            skLineSegment(sketch, "E71.MirrorCS", {"start": v(30.99, -6.35) * mm, "end": v(30.73, -6.79) * mm});
            skLineSegment(sketch, "E72.MirrorCS", {"start": v(6.86, -6.79) * mm, "end": v(6.6, -6.35) * mm});
            skLineSegment(sketch, "E73.MirrorCS", {"start": v(-1.27, -6.79) * mm, "end": v(-1.52, -6.35) * mm});
            skLineSegment(sketch, "E74.MirrorCS", {"start": v(-28.96, -6.35) * mm, "end": v(-29.21, -6.79) * mm});
            skLineSegment(sketch, "E75.MirrorCS", {"start": v(-20.57, -6.79) * mm, "end": v(-20.83, -6.35) * mm});
            skLineSegment(sketch, "E76.MirrorCS", {"start": v(7.37, -6.79) * mm, "end": v(7.11, -6.35) * mm});
            skLineSegment(sketch, "E77.MirrorCS", {"start": v(-6.86, -6.79) * mm, "end": v(-7.11, -6.35) * mm});
            skLineSegment(sketch, "E78.MirrorCS", {"start": v(-18.8, -6.35) * mm, "end": v(-19.05, -6.79) * mm});
            skLineSegment(sketch, "E79.MirrorCS", {"start": v(1.52, -6.35) * mm, "end": v(1.27, -6.79) * mm});
            skLineSegment(sketch, "E80.MirrorCS", {"start": v(10.92, -6.79) * mm, "end": v(10.67, -6.35) * mm});
            skLineSegment(sketch, "E81.MirrorCS", {"start": v(20.07, -6.79) * mm, "end": v(19.81, -6.35) * mm});
            skLineSegment(sketch, "E82.MirrorCS", {"start": v(21.08, -6.79) * mm, "end": v(20.83, -6.35) * mm});
            skLineSegment(sketch, "E83.MirrorCS", {"start": v(0.25, -6.79) * mm, "end": v(0, -6.35) * mm});
            skLineSegment(sketch, "E84.MirrorCS", {"start": v(-29.46, -6.35) * mm, "end": v(-29.72, -6.79) * mm});
            skLineSegment(sketch, "E85.MirrorCS", {"start": v(-19.3, -6.35) * mm, "end": v(-19.56, -6.79) * mm});
            skLineSegment(sketch, "E86.MirrorCS", {"start": v(22.86, -6.35) * mm, "end": v(22.6, -6.79) * mm});
            skLineSegment(sketch, "E87.MirrorCS", {"start": v(23.37, -6.35) * mm, "end": v(23.11, -6.79) * mm});
            skLineSegment(sketch, "E88.MirrorCS", {"start": v(-30.48, -6.35) * mm, "end": v(-30.73, -6.79) * mm});
            skLineSegment(sketch, "E89.MirrorCS", {"start": v(-0.25, -6.79) * mm, "end": v(-0.5, -6.35) * mm});
            skLineSegment(sketch, "E90.MirrorCS", {"start": v(18.8, -6.35) * mm, "end": v(18.54, -6.79) * mm});
            skLineSegment(sketch, "E91.MirrorCS", {"start": v(29.21, -6.79) * mm, "end": v(28.96, -6.35) * mm});
            skLineSegment(sketch, "E92.MirrorCS", {"start": v(6.1, -6.35) * mm, "end": v(5.84, -6.79) * mm});
            skLineSegment(sketch, "E93.MirrorCS", {"start": v(-26.42, -6.35) * mm, "end": v(-26.67, -6.79) * mm});
            skLineSegment(sketch, "E94.MirrorCS", {"start": v(2.03, -6.35) * mm, "end": v(1.78, -6.79) * mm});
            skLineSegment(sketch, "E95.MirrorCS", {"start": v(13.2, -6.35) * mm, "end": v(12.95, -6.79) * mm});
            skLineSegment(sketch, "E96.MirrorCS", {"start": v(3.56, -6.35) * mm, "end": v(3.3, -6.79) * mm});
            skLineSegment(sketch, "E97.MirrorCS", {"start": v(-10.92, -6.79) * mm, "end": v(-11.18, -6.35) * mm});
            skLineSegment(sketch, "E98.MirrorCS", {"start": v(6.6, -6.35) * mm, "end": v(6.35, -6.79) * mm});
            skLineSegment(sketch, "E99.MirrorCS", {"start": v(-23.88, -6.35) * mm, "end": v(-24.13, -6.79) * mm});
            skLineSegment(sketch, "E100.MirrorCS", {"start": v(-25.9, -6.35) * mm, "end": v(-26.16, -6.79) * mm});
            skLineSegment(sketch, "E101.MirrorCS", {"start": v(27.18, -6.79) * mm, "end": v(26.92, -6.35) * mm});
            skLineSegment(sketch, "E102.MirrorCS", {"start": v(3.81, -6.79) * mm, "end": v(3.56, -6.35) * mm});
            skLineSegment(sketch, "E103.MirrorCS", {"start": v(-9.4, -6.79) * mm, "end": v(-9.65, -6.35) * mm});
            skLineSegment(sketch, "E104.MirrorCS", {"start": v(-7.11, -6.35) * mm, "end": v(-7.37, -6.79) * mm});
            skLineSegment(sketch, "E105.MirrorCS", {"start": v(-8.9, -6.79) * mm, "end": v(-9.14, -6.35) * mm});
            skLineSegment(sketch, "E106.MirrorCS", {"start": v(26.42, -6.35) * mm, "end": v(26.16, -6.79) * mm});
            skLineSegment(sketch, "E107.MirrorCS", {"start": v(21.34, -6.35) * mm, "end": v(21.08, -6.79) * mm});
            skLineSegment(sketch, "E108.MirrorCS", {"start": v(-15.5, -6.79) * mm, "end": v(-15.75, -6.35) * mm});
            skLineSegment(sketch, "E109.MirrorCS", {"start": v(-13.97, -6.79) * mm, "end": v(-14.22, -6.35) * mm});
            skLineSegment(sketch, "E110.MirrorCS", {"start": v(-26.16, -6.79) * mm, "end": v(-26.42, -6.35) * mm});
            skLineSegment(sketch, "E111.MirrorCS", {"start": v(21.84, -6.35) * mm, "end": v(21.59, -6.79) * mm});
            skLineSegment(sketch, "E112.MirrorCS", {"start": v(26.16, -6.79) * mm, "end": v(25.9, -6.35) * mm});
            skLineSegment(sketch, "E113.MirrorCS", {"start": v(15.24, -6.35) * mm, "end": v(14.99, -6.79) * mm});
            skLineSegment(sketch, "E114.MirrorCS", {"start": v(-17.78, -6.35) * mm, "end": v(-18.03, -6.79) * mm});
            skLineSegment(sketch, "E115.MirrorCS", {"start": v(14.73, -6.35) * mm, "end": v(14.48, -6.79) * mm});
            skLineSegment(sketch, "E116.MirrorCS", {"start": v(4.06, -6.35) * mm, "end": v(3.81, -6.79) * mm});
            skLineSegment(sketch, "E117.MirrorCS", {"start": v(-30.23, -6.79) * mm, "end": v(-30.48, -6.35) * mm});
            skLineSegment(sketch, "E118.MirrorCS", {"start": v(18.29, -6.35) * mm, "end": v(18.03, -6.79) * mm});
            skLineSegment(sketch, "E119.MirrorCS", {"start": v(-20.32, -6.35) * mm, "end": v(-20.57, -6.79) * mm});
            skLineSegment(sketch, "E120.MirrorCS", {"start": v(6.35, -6.79) * mm, "end": v(6.1, -6.35) * mm});
            skLineSegment(sketch, "E121.MirrorCS", {"start": v(-4.32, -6.79) * mm, "end": v(-4.57, -6.35) * mm});
            skLineSegment(sketch, "E122.MirrorCS", {"start": v(-27.18, -6.79) * mm, "end": v(-27.43, -6.35) * mm});
            skLineSegment(sketch, "E123.MirrorCS", {"start": v(31.24, -6.79) * mm, "end": v(30.99, -6.35) * mm});
            skLineSegment(sketch, "E124.MirrorCS", {"start": v(-31.24, -6.79) * mm, "end": v(-31.5, -6.35) * mm});
            skLineSegment(sketch, "E125.MirrorCS", {"start": v(-10.67, -6.35) * mm, "end": v(-10.92, -6.79) * mm});
            skLineSegment(sketch, "E126.MirrorCS", {"start": v(12.95, -6.79) * mm, "end": v(12.7, -6.35) * mm});
            skLineSegment(sketch, "E127.MirrorCS", {"start": v(-3.3, -6.79) * mm, "end": v(-3.56, -6.35) * mm});
            skLineSegment(sketch, "E128.MirrorCS", {"start": v(-22.1, -6.79) * mm, "end": v(-22.35, -6.35) * mm});
            skLineSegment(sketch, "E129.MirrorCS", {"start": v(-14.99, -6.79) * mm, "end": v(-15.24, -6.35) * mm});
            skLineSegment(sketch, "E130.MirrorCS", {"start": v(22.35, -6.35) * mm, "end": v(22.1, -6.79) * mm});
            skLineSegment(sketch, "E131.MirrorCS", {"start": v(-4.83, -6.79) * mm, "end": v(-5.08, -6.35) * mm});
            skLineSegment(sketch, "E132.MirrorCS", {"start": v(-22.86, -6.35) * mm, "end": v(-23.11, -6.79) * mm});
            skLineSegment(sketch, "E133.MirrorCS", {"start": v(18.54, -6.79) * mm, "end": v(18.29, -6.35) * mm});
            skLineSegment(sketch, "E134.MirrorCS", {"start": v(8.9, -6.79) * mm, "end": v(8.64, -6.35) * mm});
            skLineSegment(sketch, "E135.MirrorCS", {"start": v(8.64, -6.35) * mm, "end": v(8.38, -6.79) * mm});
            skLineSegment(sketch, "E136.MirrorCS", {"start": v(9.4, -6.79) * mm, "end": v(9.14, -6.35) * mm});
            skLineSegment(sketch, "E137.MirrorCS", {"start": v(30.48, -6.35) * mm, "end": v(30.23, -6.79) * mm});
            skLineSegment(sketch, "E138.MirrorCS", {"start": v(7.11, -6.35) * mm, "end": v(6.86, -6.79) * mm});
            skLineSegment(sketch, "E139.MirrorCS", {"start": v(-1.78, -6.79) * mm, "end": v(-2.03, -6.35) * mm});
            skLineSegment(sketch, "E140.MirrorCS", {"start": v(28.96, -6.35) * mm, "end": v(28.7, -6.79) * mm});
            skLineSegment(sketch, "E141.MirrorCS", {"start": v(-6.6, -6.35) * mm, "end": v(-6.86, -6.79) * mm});
            skLineSegment(sketch, "E142.MirrorCS", {"start": v(12.45, -6.79) * mm, "end": v(12.2, -6.35) * mm});
            skLineSegment(sketch, "E143.MirrorCS", {"start": v(-6.1, -6.35) * mm, "end": v(-6.35, -6.79) * mm});
            skLineSegment(sketch, "E144.MirrorCS", {"start": v(-14.48, -6.79) * mm, "end": v(-14.73, -6.35) * mm});
            skLineSegment(sketch, "E145.MirrorCS", {"start": v(8.13, -6.35) * mm, "end": v(7.87, -6.79) * mm});
            skLineSegment(sketch, "E146.MirrorCS", {"start": v(-8.64, -6.35) * mm, "end": v(-8.9, -6.79) * mm});
            skLineSegment(sketch, "E147.MirrorCS", {"start": v(-24.38, -6.35) * mm, "end": v(-24.64, -6.79) * mm});
            skLineSegment(sketch, "E148.MirrorCS", {"start": v(-7.62, -6.35) * mm, "end": v(-7.87, -6.79) * mm});
            skLineSegment(sketch, "E149.MirrorCS", {"start": v(-23.62, -6.79) * mm, "end": v(-23.88, -6.35) * mm});
            skLineSegment(sketch, "E150.MirrorCS", {"start": v(-25.4, -6.35) * mm, "end": v(-25.65, -6.79) * mm});
            skLineSegment(sketch, "E151.MirrorCS", {"start": v(30.23, -6.79) * mm, "end": v(29.97, -6.35) * mm});
            skLineSegment(sketch, "E152.MirrorCS", {"start": v(-1.52, -6.35) * mm, "end": v(-1.78, -6.79) * mm});
            skLineSegment(sketch, "E153.MirrorCS", {"start": v(-19.81, -6.35) * mm, "end": v(-20.07, -6.79) * mm});
            skLineSegment(sketch, "E154.MirrorCS", {"start": v(-18.29, -6.35) * mm, "end": v(-18.54, -6.79) * mm});
            skLineSegment(sketch, "E155.MirrorCS", {"start": v(-24.9, -6.35) * mm, "end": v(-25.15, -6.79) * mm});
            skLineSegment(sketch, "E156.MirrorCS", {"start": v(-29.21, -6.79) * mm, "end": v(-29.46, -6.35) * mm});
            skLineSegment(sketch, "E157.MirrorCS", {"start": v(-13.46, -6.79) * mm, "end": v(-13.72, -6.35) * mm});
            skLineSegment(sketch, "E158.MirrorCS", {"start": v(17.78, -6.35) * mm, "end": v(17.53, -6.79) * mm});
            skLineSegment(sketch, "E159.MirrorCS", {"start": v(-29.72, -6.79) * mm, "end": v(-29.97, -6.35) * mm});
            skLineSegment(sketch, "E160.MirrorCS", {"start": v(-8.38, -6.79) * mm, "end": v(-8.64, -6.35) * mm});
            skLineSegment(sketch, "E161.MirrorCS", {"start": v(-17.27, -6.35) * mm, "end": v(-17.53, -6.79) * mm});
            skLineSegment(sketch, "E162.MirrorCS", {"start": v(-12.7, -6.35) * mm, "end": v(-12.95, -6.79) * mm});
            skLineSegment(sketch, "E163.MirrorCS", {"start": v(7.87, -6.79) * mm, "end": v(7.62, -6.35) * mm});
            skLineSegment(sketch, "E164.MirrorCS", {"start": v(-11.94, -6.79) * mm, "end": v(-12.2, -6.35) * mm});
            skLineSegment(sketch, "E165.MirrorCS", {"start": v(-18.54, -6.79) * mm, "end": v(-18.8, -6.35) * mm});
            skLineSegment(sketch, "E166.MirrorCS", {"start": v(13.72, -6.35) * mm, "end": v(13.46, -6.79) * mm});
            skLineSegment(sketch, "E167.MirrorCS", {"start": v(20.83, -6.35) * mm, "end": v(20.57, -6.79) * mm});
            skLineSegment(sketch, "E168.MirrorCS", {"start": v(-20.07, -6.79) * mm, "end": v(-20.32, -6.35) * mm});
            skLineSegment(sketch, "E169.MirrorCS", {"start": v(-11.68, -6.35) * mm, "end": v(-11.94, -6.79) * mm});
            skLineSegment(sketch, "E170.MirrorCS", {"start": v(-5.33, -6.79) * mm, "end": v(-5.59, -6.35) * mm});
            skLineSegment(sketch, "E171.MirrorCS", {"start": v(16, -6.79) * mm, "end": v(15.75, -6.35) * mm});
            skLineSegment(sketch, "E172.MirrorCS", {"start": v(-9.65, -6.35) * mm, "end": v(-9.9, -6.79) * mm});
            skLineSegment(sketch, "E173.MirrorCS", {"start": v(27.69, -6.79) * mm, "end": v(27.43, -6.35) * mm});
            skLineSegment(sketch, "E174.MirrorCS", {"start": v(25.9, -6.35) * mm, "end": v(25.65, -6.79) * mm});
            skLineSegment(sketch, "E175.MirrorCS", {"start": v(17.02, -6.79) * mm, "end": v(16.76, -6.35) * mm});
            skLineSegment(sketch, "E176.MirrorCS", {"start": v(-11.18, -6.35) * mm, "end": v(-11.43, -6.79) * mm});
            skLineSegment(sketch, "E177.MirrorCS", {"start": v(14.22, -6.35) * mm, "end": v(13.97, -6.79) * mm});
            skLineSegment(sketch, "E178.MirrorCS", {"start": v(-22.6, -6.79) * mm, "end": v(-22.86, -6.35) * mm});
            skLineSegment(sketch, "E179.MirrorCS", {"start": v(9.9, -6.79) * mm, "end": v(9.65, -6.35) * mm});
            skLineSegment(sketch, "E180.MirrorCS", {"start": v(12.7, -6.35) * mm, "end": v(12.45, -6.79) * mm});
            skLineSegment(sketch, "E181.MirrorCS", {"start": v(17.53, -6.79) * mm, "end": v(17.27, -6.35) * mm});
            skLineSegment(sketch, "E182.MirrorCS", {"start": v(-19.05, -6.79) * mm, "end": v(-19.3, -6.35) * mm});
            skLineSegment(sketch, "E183.MirrorCS", {"start": v(14.48, -6.79) * mm, "end": v(14.22, -6.35) * mm});
            skLineSegment(sketch, "E184.MirrorCS", {"start": v(-9.9, -6.79) * mm, "end": v(-10.16, -6.35) * mm});
            skLineSegment(sketch, "E185.MirrorCS", {"start": v(18.03, -6.79) * mm, "end": v(17.78, -6.35) * mm});
            skLineSegment(sketch, "E186.MirrorCS", {"start": v(13.46, -6.79) * mm, "end": v(13.2, -6.35) * mm});
            skLineSegment(sketch, "E187.MirrorCS", {"start": v(13.97, -6.79) * mm, "end": v(13.72, -6.35) * mm});
            skLineSegment(sketch, "E188.MirrorCS", {"start": v(-21.08, -6.79) * mm, "end": v(-21.34, -6.35) * mm});
            skLineSegment(sketch, "E189.MirrorCS", {"start": v(-27.43, -6.35) * mm, "end": v(-27.69, -6.79) * mm});
            skLineSegment(sketch, "E190.MirrorCS", {"start": v(11.68, -6.35) * mm, "end": v(11.43, -6.79) * mm});
            skLineSegment(sketch, "E191.MirrorCS", {"start": v(11.18, -6.35) * mm, "end": v(10.92, -6.79) * mm});
            skLineSegment(sketch, "E192.MirrorCS", {"start": v(-19.56, -6.79) * mm, "end": v(-19.81, -6.35) * mm});
            skLineSegment(sketch, "E193.MirrorCS", {"start": v(-4.57, -6.35) * mm, "end": v(-4.83, -6.79) * mm});
            skLineSegment(sketch, "E194.MirrorCS", {"start": v(16.76, -6.35) * mm, "end": v(16.51, -6.79) * mm});
            skLineSegment(sketch, "E195.MirrorCS", {"start": v(-5.59, -6.35) * mm, "end": v(-5.84, -6.79) * mm});
            skLineSegment(sketch, "E196.MirrorCS", {"start": v(23.62, -6.79) * mm, "end": v(23.37, -6.35) * mm});
            skLineSegment(sketch, "E197.MirrorCS", {"start": v(25.65, -6.79) * mm, "end": v(25.4, -6.35) * mm});
            skLineSegment(sketch, "E198.MirrorCS", {"start": v(-7.87, -6.79) * mm, "end": v(-8.13, -6.35) * mm});
            skLineSegment(sketch, "E199.MirrorCS", {"start": v(30.73, -6.79) * mm, "end": v(30.48, -6.35) * mm});
            skLineSegment(sketch, "E200.MirrorCS", {"start": v(16.26, -6.35) * mm, "end": v(16, -6.79) * mm});
            skLineSegment(sketch, "E201.MirrorCS", {"start": v(-30.99, -6.35) * mm, "end": v(-31.24, -6.79) * mm});
            skLineSegment(sketch, "E202.MirrorCS", {"start": v(10.67, -6.35) * mm, "end": v(10.41, -6.79) * mm});
            skLineSegment(sketch, "E203.MirrorCS", {"start": v(-16.76, -6.35) * mm, "end": v(-17.02, -6.79) * mm});
            skLineSegment(sketch, "E204.MirrorCS", {"start": v(23.11, -6.79) * mm, "end": v(22.86, -6.35) * mm});
            skLineSegment(sketch, "E205.MirrorCS", {"start": v(-13.2, -6.35) * mm, "end": v(-13.46, -6.79) * mm});
            skLineSegment(sketch, "E206.MirrorCS", {"start": v(24.9, -6.35) * mm, "end": v(24.64, -6.79) * mm});
            skLineSegment(sketch, "E207.MirrorCS", {"start": v(-3.81, -6.79) * mm, "end": v(-4.06, -6.35) * mm});
            skLineSegment(sketch, "E208.MirrorCS", {"start": v(-20.83, -6.35) * mm, "end": v(-21.08, -6.79) * mm});
            skLineSegment(sketch, "E209.MirrorCS", {"start": v(-29.97, -6.35) * mm, "end": v(-30.23, -6.79) * mm});
            skLineSegment(sketch, "E210.MirrorCS", {"start": v(-21.34, -6.35) * mm, "end": v(-21.6, -6.79) * mm});
            skLineSegment(sketch, "E211.MirrorCS", {"start": v(29.46, -6.35) * mm, "end": v(29.21, -6.79) * mm});
            skLineSegment(sketch, "E212.MirrorCS", {"start": v(28.2, -6.79) * mm, "end": v(27.94, -6.35) * mm});
            skLineSegment(sketch, "E213.MirrorCS", {"start": v(24.38, -6.35) * mm, "end": v(24.13, -6.79) * mm});
            skLineSegment(sketch, "E214.MirrorCS", {"start": v(-31.75, -6.79) * mm, "end": v(-32, -6.35) * mm});
            skLineSegment(sketch, "E215.MirrorCS", {"start": v(-16, -6.79) * mm, "end": v(-16.26, -6.35) * mm});
            skLineSegment(sketch, "E216.MirrorCS", {"start": v(-26.67, -6.79) * mm, "end": v(-26.92, -6.35) * mm});
            skLineSegment(sketch, "E217.MirrorCS", {"start": v(9.65, -6.35) * mm, "end": v(9.4, -6.79) * mm});
            skLineSegment(sketch, "E218.MirrorCS", {"start": v(-26.92, -6.35) * mm, "end": v(-27.18, -6.79) * mm});
            skLineSegment(sketch, "E219.MirrorCS", {"start": v(10.41, -6.79) * mm, "end": v(10.16, -6.35) * mm});
            skLineSegment(sketch, "E220.MirrorCS", {"start": v(29.97, -6.35) * mm, "end": v(29.72, -6.79) * mm});
            skLineSegment(sketch, "E221.MirrorCS", {"start": v(-10.41, -6.79) * mm, "end": v(-10.67, -6.35) * mm});
            skLineSegment(sketch, "E222.MirrorCS", {"start": v(-18.03, -6.79) * mm, "end": v(-18.29, -6.35) * mm});
            skLineSegment(sketch, "E223.MirrorCS", {"start": v(-13.72, -6.35) * mm, "end": v(-13.97, -6.79) * mm});
            skLineSegment(sketch, "E224.MirrorCS", {"start": v(21.6, -6.79) * mm, "end": v(21.34, -6.35) * mm});
            skLineSegment(sketch, "E225.MirrorCS", {"start": v(-31.5, -6.35) * mm, "end": v(-31.75, -6.79) * mm});
            skLineSegment(sketch, "E226.MirrorCS", {"start": v(27.94, -6.35) * mm, "end": v(27.69, -6.79) * mm});
            skLineSegment(sketch, "E227.MirrorCS", {"start": v(20.57, -6.79) * mm, "end": v(20.32, -6.35) * mm});
            skLineSegment(sketch, "E228.MirrorCS", {"start": v(-23.37, -6.35) * mm, "end": v(-23.62, -6.79) * mm});
            skLineSegment(sketch, "E229.MirrorCS", {"start": v(-6.35, -6.79) * mm, "end": v(-6.6, -6.35) * mm});
            skLineSegment(sketch, "E230.MirrorCS", {"start": v(-12.45, -6.79) * mm, "end": v(-12.7, -6.35) * mm});
            skLineSegment(sketch, "E231.MirrorCS", {"start": v(24.13, -6.79) * mm, "end": v(23.88, -6.35) * mm});
            skLineSegment(sketch, "E232.MirrorCS", {"start": v(-30.73, -6.79) * mm, "end": v(-30.99, -6.35) * mm});
            skLineSegment(sketch, "E233.MirrorCS", {"start": v(-16.51, -6.79) * mm, "end": v(-16.76, -6.35) * mm});
            skLineSegment(sketch, "E234.MirrorCS", {"start": v(-14.22, -6.35) * mm, "end": v(-14.48, -6.79) * mm});
            skLineSegment(sketch, "E235.MirrorCS", {"start": v(10.16, -6.35) * mm, "end": v(9.9, -6.79) * mm});
            skLineSegment(sketch, "E236.MirrorCS", {"start": v(15.75, -6.35) * mm, "end": v(15.5, -6.79) * mm});
            skLineSegment(sketch, "E237.MirrorCS", {"start": v(12.2, -6.35) * mm, "end": v(11.94, -6.79) * mm});
            skLineSegment(sketch, "E238.MirrorCS", {"start": v(7.62, -6.35) * mm, "end": v(7.37, -6.79) * mm});
            skLineSegment(sketch, "E239.MirrorCS", {"start": v(-10.16, -6.35) * mm, "end": v(-10.41, -6.79) * mm});
            skLineSegment(sketch, "E240.MirrorCS", {"start": v(-17.53, -6.79) * mm, "end": v(-17.78, -6.35) * mm});
            skLineSegment(sketch, "E241.MirrorCS", {"start": v(-5.84, -6.79) * mm, "end": v(-6.1, -6.35) * mm});
            skLineSegment(sketch, "E242.MirrorCS", {"start": v(-23.11, -6.79) * mm, "end": v(-23.37, -6.35) * mm});
            skLineSegment(sketch, "E243.MirrorCS", {"start": v(31.75, -6.79) * mm, "end": v(31.5, -6.35) * mm});
            skLineSegment(sketch, "E244.MirrorCS", {"start": v(22.6, -6.79) * mm, "end": v(22.35, -6.35) * mm});
            skLineSegment(sketch, "E245.MirrorCS", {"start": v(24.64, -6.79) * mm, "end": v(24.38, -6.35) * mm});
            skLineSegment(sketch, "E246.MirrorCS", {"start": v(26.67, -6.79) * mm, "end": v(26.42, -6.35) * mm});
            skLineSegment(sketch, "E247.MirrorCS", {"start": v(25.4, -6.35) * mm, "end": v(25.15, -6.79) * mm});
            skLineSegment(sketch, "E248.MirrorCS", {"start": v(22.1, -6.79) * mm, "end": v(21.84, -6.35) * mm});
            skLineSegment(sketch, "E249.MirrorCS", {"start": v(29.72, -6.79) * mm, "end": v(29.46, -6.35) * mm});
            skLineSegment(sketch, "E250.MirrorCS", {"start": v(-2.03, -6.35) * mm, "end": v(-2.29, -6.79) * mm});
            skLineSegment(sketch, "E251.MirrorCS", {"start": v(-21.84, -6.35) * mm, "end": v(-22.1, -6.79) * mm});
            skLineSegment(sketch, "E252.MirrorCS", {"start": v(23.88, -6.35) * mm, "end": v(23.62, -6.79) * mm});
            skLineSegment(sketch, "E253.MirrorCS", {"start": v(32, -6.35) * mm, "end": v(31.75, -6.79) * mm});
            skLineSegment(sketch, "E254.MirrorCS", {"start": v(-15.75, -6.35) * mm, "end": v(-16, -6.79) * mm});
            skLineSegment(sketch, "E255.MirrorCS", {"start": v(-2.54, -6.35) * mm, "end": v(-2.8, -6.79) * mm});
            skLineSegment(sketch, "E256.MirrorCS", {"start": v(-3.56, -6.35) * mm, "end": v(-3.81, -6.79) * mm});
            skLineSegment(sketch, "E257.MirrorCS", {"start": v(32.26, -6.79) * mm, "end": v(32, -6.35) * mm});
            skLineSegment(sketch, "E258.MirrorCS", {"start": v(-25.15, -6.79) * mm, "end": v(-25.4, -6.35) * mm});
            skLineSegment(sketch, "E259.MirrorCS", {"start": v(-2.29, -6.79) * mm, "end": v(-2.54, -6.35) * mm});
            skLineSegment(sketch, "E260.MirrorCS", {"start": v(-32, -6.35) * mm, "end": v(-32.26, -6.79) * mm});
            skLineSegment(sketch, "E261.MirrorCS", {"start": v(-32.26, -6.79) * mm, "end": v(-32.51, -6.35) * mm});
            skLineSegment(sketch, "E262.MirrorCS", {"start": v(28.45, -6.35) * mm, "end": v(28.2, -6.79) * mm});
            skLineSegment(sketch, "E263.MirrorCS", {"start": v(11.94, -6.79) * mm, "end": v(11.68, -6.35) * mm});
            skLineSegment(sketch, "E264.MirrorCS", {"start": v(-2.8, -6.79) * mm, "end": v(-3.05, -6.35) * mm});
            skLineSegment(sketch, "E265.MirrorCS", {"start": v(-25.65, -6.79) * mm, "end": v(-25.9, -6.35) * mm});
            skLineSegment(sketch, "E266.MirrorCS", {"start": v(-3.05, -6.35) * mm, "end": v(-3.3, -6.79) * mm});
            skLineSegment(sketch, "E267.MirrorCS", {"start": v(8.38, -6.79) * mm, "end": v(8.13, -6.35) * mm});
            skLineSegment(sketch, "E268.MirrorCS", {"start": v(-16.26, -6.35) * mm, "end": v(-16.51, -6.79) * mm});
            skLineSegment(sketch, "E269.MirrorCS", {"start": v(4.32, -6.79) * mm, "end": v(4.06, -6.35) * mm});
            skLineSegment(sketch, "E270.MirrorCS", {"start": v(-21.59, -6.79) * mm, "end": v(-21.84, -6.35) * mm});
            skLineSegment(sketch, "E271.MirrorCS", {"start": v(16.51, -6.79) * mm, "end": v(16.26, -6.35) * mm});
            skLineSegment(sketch, "E272.MirrorCS", {"start": v(28.7, -6.79) * mm, "end": v(28.45, -6.35) * mm});
            skLineSegment(sketch, "E273.MirrorCS", {"start": v(32.51, -6.1) * mm, "end": v(32.51, -6.35) * mm});
            skLineSegment(sketch, "E274.MirrorCS", {"start": v(-32.51, -6.1) * mm, "end": v(32.51, -6.1) * mm});
            skLineSegment(sketch, "E275.MirrorCS", {"start": v(-32.51, -6.35) * mm, "end": v(-32.51, -6.1) * mm});
            skLineSegment(sketch, "E276.MirrorCS", {"start": v(32.51, -6.35) * mm, "end": v(32.26, -6.79) * mm});
            skSolve(sketch);
        }
        {
            var Q0;
            Q0=qSketchRegion(id+"F2",true);
            extrude(context, id + "F3", {"entities" : qUnion([Q0]), "operationType" : NewBodyOperationType.REMOVE, "endBound" : BoundingType.SYMMETRIC, "oppositeDirection" : true, "depth" : 25.4 * mm, "offsetDistance" : 25.4 * mm});
        }
        {
            var Q0;
            Q0=makeQuery(id+"F1.opExtrude","SWEPT_EDGE",EDGE,{"disambiguationData":[OSD([sQuery(id+"F0.wireOp",EDGE,"E0.top"),sQuery(id+"F0.wireOp",EDGE,"E3.trimOffspring")])]});
            var Q1;
            Q1=makeQuery(id+"F1.opExtrude","SWEPT_EDGE",EDGE,{"disambiguationData":[OSD([sQuery(id+"F0.wireOp",EDGE,"E0.top"),sQuery(id+"F0.wireOp",EDGE,"E2.trimOffspring")])]});
            var Q2;
            Q2=makeQuery(id+"F1.opExtrude","SWEPT_EDGE",EDGE,{"disambiguationData":[OSD([sQuery(id+"F0.wireOp",EDGE,"E0.bottom"),sQuery(id+"F0.wireOp",EDGE,"E0.left")])]});
            var Q3;
            Q3=makeQuery(id+"F1.opExtrude","SWEPT_EDGE",EDGE,{"disambiguationData":[OSD([sQuery(id+"F0.wireOp",EDGE,"E0.bottom"),sQuery(id+"F0.wireOp",EDGE,"E0.right")])]});
            fillet(context, id + "F4", {"entities" : qUnion([Q0, Q1, Q2, Q3]), "radius" : 5.08 * mm, "tangentPropagation" : true, "allowEdgeOverflow" : false});
        }
        {
            var Q0;
            Q0=makeQuery(id+"F1.opExtrude","CAP_EDGE",EDGE,{"disambiguationData":[OSD([sQuery(id+"F0.wireOp",EDGE,"E0.top")])],"isStart":false});
            var Q1;
            Q1=makeQuery(id+"F1.opExtrude","CAP_EDGE",EDGE,{"disambiguationData":[OSD([sQuery(id+"F0.wireOp",EDGE,"E0.top")])],"isStart":true});
            var Q2;
            Q2=makeQuery(id+"F1.opExtrude","CAP_EDGE",EDGE,{"disambiguationData":[OSD([sQuery(id+"F0.wireOp",EDGE,"E0.bottom")])],"isStart":false});
            var Q3;
            Q3=makeQuery(id+"F1.opExtrude","CAP_EDGE",EDGE,{"disambiguationData":[OSD([sQuery(id+"F0.wireOp",EDGE,"E0.bottom")])],"isStart":true});
            fillet(context, id + "F5", {"entities" : qUnion([Q0, Q1, Q2, Q3]), "radius" : 0.5 * mm, "tangentPropagation" : true, "allowEdgeOverflow" : false});
        }
    });
